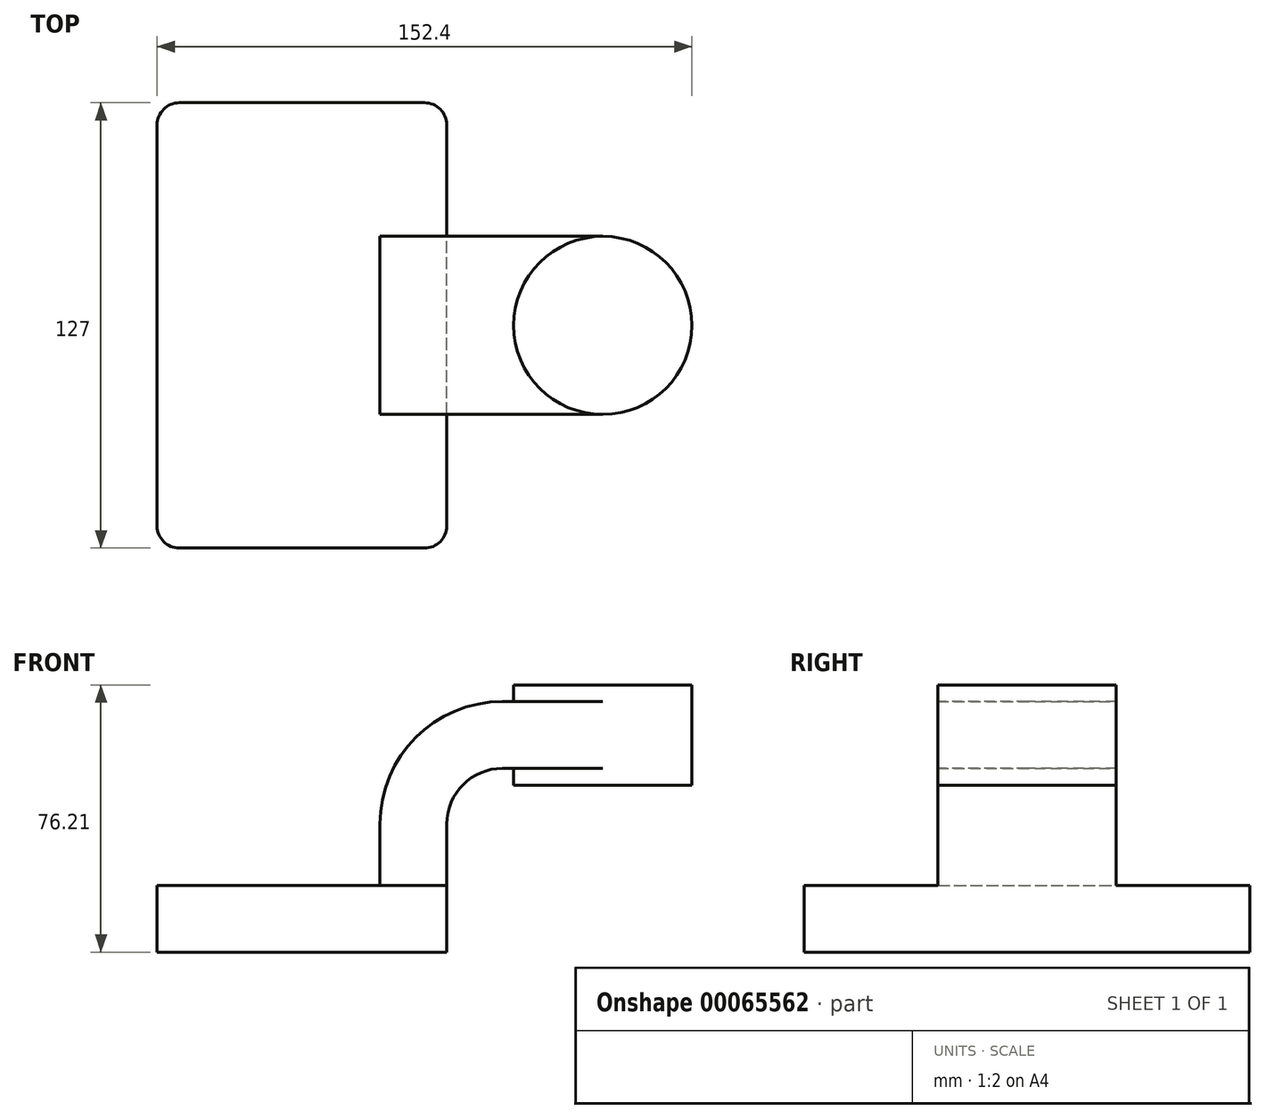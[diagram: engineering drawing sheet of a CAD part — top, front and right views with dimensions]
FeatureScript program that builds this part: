
annotation { "Feature Type Name" : "Feature", "Feature Type Description" : "" }
export const myFeature = defineFeature(function(context is Context, id is Id, definition is map)
    precondition{}
    {
        {
            var Q0;
            Q0=qCreatedBy(makeId("Front.planeOp"),FACE);
            var sketch = newSketch(context, id + "F0", { "sketchPlane" : qUnion([Q0])});
            skLineSegment(sketch, "E0.bottom", {"start": v(-41.28, 9.52) * mm, "end": v(41.27, 9.53) * mm});
            skLineSegment(sketch, "E0.top", {"start": v(-41.28, -9.53) * mm, "end": v(41.28, -9.53) * mm});
            skLineSegment(sketch, "E0.left", {"start": v(-41.28, 9.52) * mm, "end": v(-41.28, -9.53) * mm});
            skLineSegment(sketch, "E0.right", {"start": v(41.27, 9.53) * mm, "end": v(41.28, -9.52) * mm});
            skPoint(sketch, "E0.middle", {"position": v(0, 0) * mm});
            skLineSegment(sketch, "E1.bottom", {"start": v(111.12, 66.67) * mm, "end": v(60.32, 66.67) * mm});
            skLineSegment(sketch, "E1.top", {"start": v(111.12, 38.1) * mm, "end": v(60.33, 38.1) * mm});
            skLineSegment(sketch, "E1.left", {"start": v(111.12, 66.67) * mm, "end": v(111.12, 38.1) * mm});
            skLineSegment(sketch, "E1.right", {"start": v(60.32, 66.67) * mm, "end": v(60.33, 38.1) * mm});
            skPoint(sketch, "E1.middle", {"position": v(85.72, 52.39) * mm});
            skLineSegment(sketch, "E2", {"start": v(41.27, 9.53) * mm, "end": v(41.27, 27) * mm});
            skArc(sketch, "E3", {"start": v(41.27, 27) * mm, "mid": v(45.92, 38.23) * mm, "end": v(57.15, 42.88) * mm});
            skLineSegment(sketch, "E4", {"start": v(57.15, 42.88) * mm, "end": v(85.93, 42.88) * mm});
            skLineSegment(sketch, "E5.0", {"start": v(57.15, 61.93) * mm, "end": v(85.93, 61.93) * mm});
            skArc(sketch, "E5.1", {"start": v(22.22, 27) * mm, "mid": v(32.45, 51.7) * mm, "end": v(57.15, 61.93) * mm});
            skLineSegment(sketch, "E5.2", {"start": v(22.22, 9.53) * mm, "end": v(22.22, 27) * mm});
            skLineSegment(sketch, "E6", {"start": v(85.72, 38.1) * mm, "end": v(85.72, 66.67) * mm});
            skFitSpline(sketch, "E7", {"points": [v(-41.28, 9.52) * mm, v(57.15, 61.93) * mm], "startDerivative": vector(25.65, 97.08) * mm, "endDerivative": vector(104.67, -12.62) * mm});
            skSolve(sketch);
        }
        {
            var Q0;
            Q0=makeQuery(id+"F0.imprint","IMPRINT",FACE,{"disambiguationData":[TD([[makeQuery(id+"F0.imprint","IMPRINT",EDGE,{"derivedFrom":sQuery(id+"F0.wireOp",EDGE,"E0.top")}),1.0]])]});
            extrude(context, id + "F1", {"entities" : qUnion([Q0]), "endBound" : BoundingType.SYMMETRIC, "depth" : 127 * mm});
        }
        {
            var Q0;
            {var subQ1=sQuery(id+"F0.wireOp",EDGE,"E2");Q0=makeQuery(id+"F0.imprint","IMPRINT",FACE,{"disambiguationData":[TD([[makeQuery(id+"F0.imprint","IMPRINT",EDGE,{"derivedFrom":subQ1}),1.0]])]});}
            var Q1;
            {var subQ0=sQuery(id+"F0.wireOp",EDGE,"E5.0");var subQ1=sQuery(id+"F0.wireOp",EDGE,"E1.right");var subQ2=makeQuery(id+"F0.imprint","INTERSECT",VERTEX,{"derivedFrom":[subQ1,subQ0]});Q1=makeQuery(id+"F0.imprint","IMPRINT",FACE,{"disambiguationData":[TD([[makeQuery(id+"F0.imprint","IMPRINT",EDGE,{"disambiguationData":[TD([[subQ2,-1.0]])],"derivedFrom":subQ1}),1.0]])]});}
            extrude(context, id + "F2", {"entities" : qUnion([Q0, Q1]), "operationType" : NewBodyOperationType.ADD, "endBound" : BoundingType.SYMMETRIC, "depth" : 50.8 * mm});
        }
        {
            var Q0;
            Q0=makeQuery(id+"F0.imprint","IMPRINT",FACE,{"disambiguationData":[TD([[makeQuery(id+"F0.imprint","IMPRINT",EDGE,{"derivedFrom":sQuery(id+"F0.wireOp",EDGE,"E5.1")}),1.0]])]});
            extrude(context, id + "F3", {"entities" : qUnion([Q0]), "operationType" : NewBodyOperationType.ADD, "endBound" : BoundingType.SYMMETRIC, "depth" : 15.88 * mm});
        }
        {
            var Q0;
            {var subQ0=sQuery(id+"F0.wireOp",EDGE,"E1.left");Q0=makeQuery(id+"F0.imprint","IMPRINT",FACE,{"disambiguationData":[TD([[makeQuery(id+"F0.imprint","IMPRINT",EDGE,{"derivedFrom":subQ0}),-1.0]])]});}
            var Q1;
            Q1=sQuery(id+"F0.wireOp",EDGE,"E6");
            revolve(context, id + "F4", {"operationType" : NewBodyOperationType.ADD, "entities" : qUnion([Q0]), "axis" : qUnion([Q1]), "revolveType" : RevolveType.FULL});
        }
        {
            var Q0;
            Q0=makeQuery(id+"F1.opExtrude","CAP_EDGE",EDGE,{"disambiguationData":[OSD([sQuery(id+"F0.wireOp",EDGE,"E0.left")])],"isStart":false});
            var Q1;
            Q1=makeQuery(id+"F1.opExtrude","CAP_EDGE",EDGE,{"disambiguationData":[OSD([sQuery(id+"F0.wireOp",EDGE,"E0.right")])],"isStart":false});
            var Q2;
            Q2=makeQuery(id+"F1.opExtrude","CAP_EDGE",EDGE,{"disambiguationData":[OSD([sQuery(id+"F0.wireOp",EDGE,"E0.right")])],"isStart":true});
            var Q3;
            Q3=makeQuery(id+"F1.opExtrude","CAP_EDGE",EDGE,{"disambiguationData":[OSD([sQuery(id+"F0.wireOp",EDGE,"E0.left")])],"isStart":true});
            fillet(context, id + "F5", {"entities" : qUnion([Q0, Q1, Q2, Q3]), "radius" : 6.35 * mm, "tangentPropagation" : true, "allowEdgeOverflow" : false});
        }
    });
